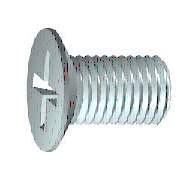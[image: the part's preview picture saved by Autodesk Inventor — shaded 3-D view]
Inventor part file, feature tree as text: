
AUTODESK INVENTOR PART (.ipt)
format: ipt  version: 2017 (Build 210142000, 142)  size: 243,712 bytes
history: native  units: mm (DEFAULTED — no unit token found)
features: sketch x2, other x1, extrude x1, plane x1
ambient origin geometry x7: Origin, YZ Plane, XZ Plane, X Axis, Y Axis, Z Axis, Center Point
bodies: Solid1 (feature_tree)
feature tree (5):
  sketch  "Esquisse1"
  other  "Corps"
  extrude  "Rainure"  Depth=5.35mm
  plane  "Work Plane2"
  sketch  "Esquisse2"
